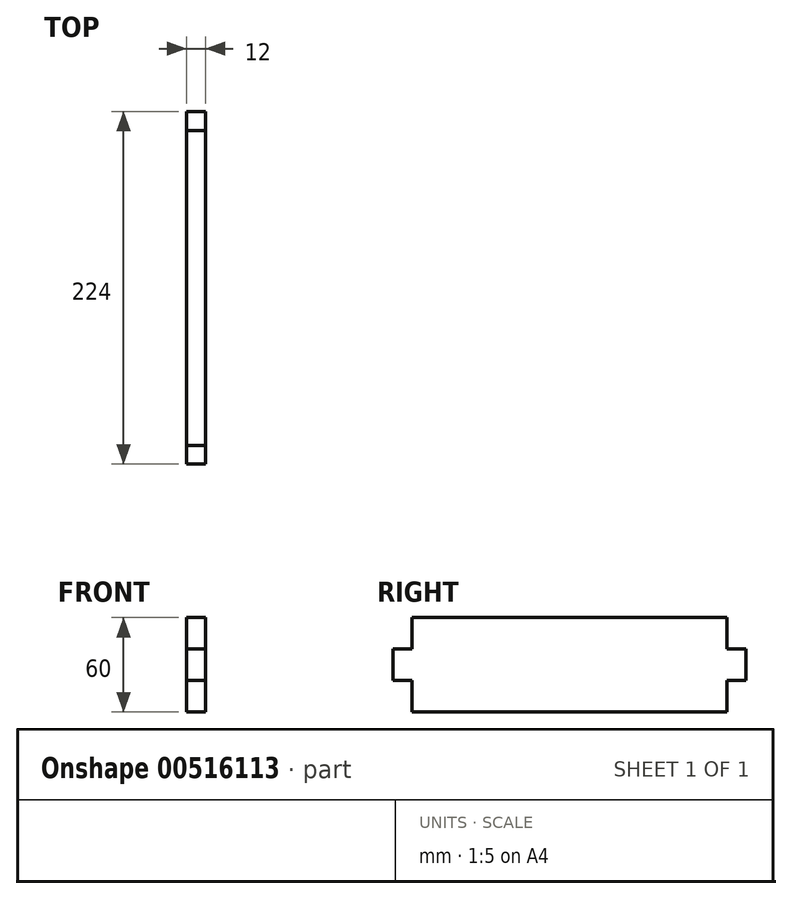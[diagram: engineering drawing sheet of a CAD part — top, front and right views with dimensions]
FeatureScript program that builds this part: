
annotation { "Feature Type Name" : "Feature", "Feature Type Description" : "" }
export const myFeature = defineFeature(function(context is Context, id is Id, definition is map)
    precondition{}
    {
        {
            var Q0;
            Q0=qCreatedBy(makeId("Right.planeOp"),FACE);
            var sketch = newSketch(context, id + "F0", { "sketchPlane" : qUnion([Q0])});
            skLineSegment(sketch, "E0", {"start": v(12, 0) * mm, "end": v(12, 20) * mm});
            skLineSegment(sketch, "E1", {"start": v(12, 20) * mm, "end": v(0, 20) * mm});
            skLineSegment(sketch, "E2", {"start": v(0, 20) * mm, "end": v(0, 40) * mm});
            skLineSegment(sketch, "E3", {"start": v(0, 40) * mm, "end": v(12, 40) * mm});
            skLineSegment(sketch, "E4", {"start": v(12, 40) * mm, "end": v(12, 60) * mm});
            skLineSegment(sketch, "E5", {"start": v(12, 60) * mm, "end": v(112, 60) * mm});
            skLineSegment(sketch, "E6", {"start": v(112, 60) * mm, "end": v(112, 0) * mm, "construction": true});
            skLineSegment(sketch, "E7", {"start": v(112, 0) * mm, "end": v(12, 0) * mm});
            skLineSegment(sketch, "E8.MirrorCS", {"start": v(224, 20) * mm, "end": v(224, 40) * mm});
            skLineSegment(sketch, "E9.MirrorCS", {"start": v(224, 40) * mm, "end": v(212, 40) * mm});
            skLineSegment(sketch, "E10.MirrorCS", {"start": v(212, 0) * mm, "end": v(212, 20) * mm});
            skLineSegment(sketch, "E11.MirrorCS", {"start": v(212, 20) * mm, "end": v(224, 20) * mm});
            skLineSegment(sketch, "E12.MirrorCS", {"start": v(212, 60) * mm, "end": v(112, 60) * mm});
            skLineSegment(sketch, "E13.MirrorCS", {"start": v(212, 40) * mm, "end": v(212, 60) * mm});
            skLineSegment(sketch, "E14.MirrorCS", {"start": v(112, 0) * mm, "end": v(212, 0) * mm});
            skSolve(sketch);
        }
        {
            var Q0;
            Q0 = qSketchRegion(id + "F0", true);
            extrude(context, id + "F1", {"entities" : qUnion([Q0]), "depth" : 12 * mm, "offsetDistance" : 25 * mm});
        }
    });
